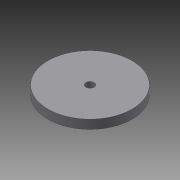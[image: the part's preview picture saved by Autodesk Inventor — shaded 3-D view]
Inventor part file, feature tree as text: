
AUTODESK INVENTOR PART (.ipt)
format: ipt  version: 2015 (Build 190159000, 159)  size: 73,216 bytes
history: native  units: mm
features: extrude x1, sketch x1
ambient origin geometry x8: Origin, YZ Plane, XZ Plane, XY Plane, X Axis, Y Axis, Z Axis, Center Point
bodies: Solid1 (feature_tree)
feature tree (2):
  extrude  "Extrusion1"  Depth=3.0mm
  sketch  "Sketch1"  dims[d0=28.5mm d3=2.8mm d4=3.0mm d5=0.0mm]
